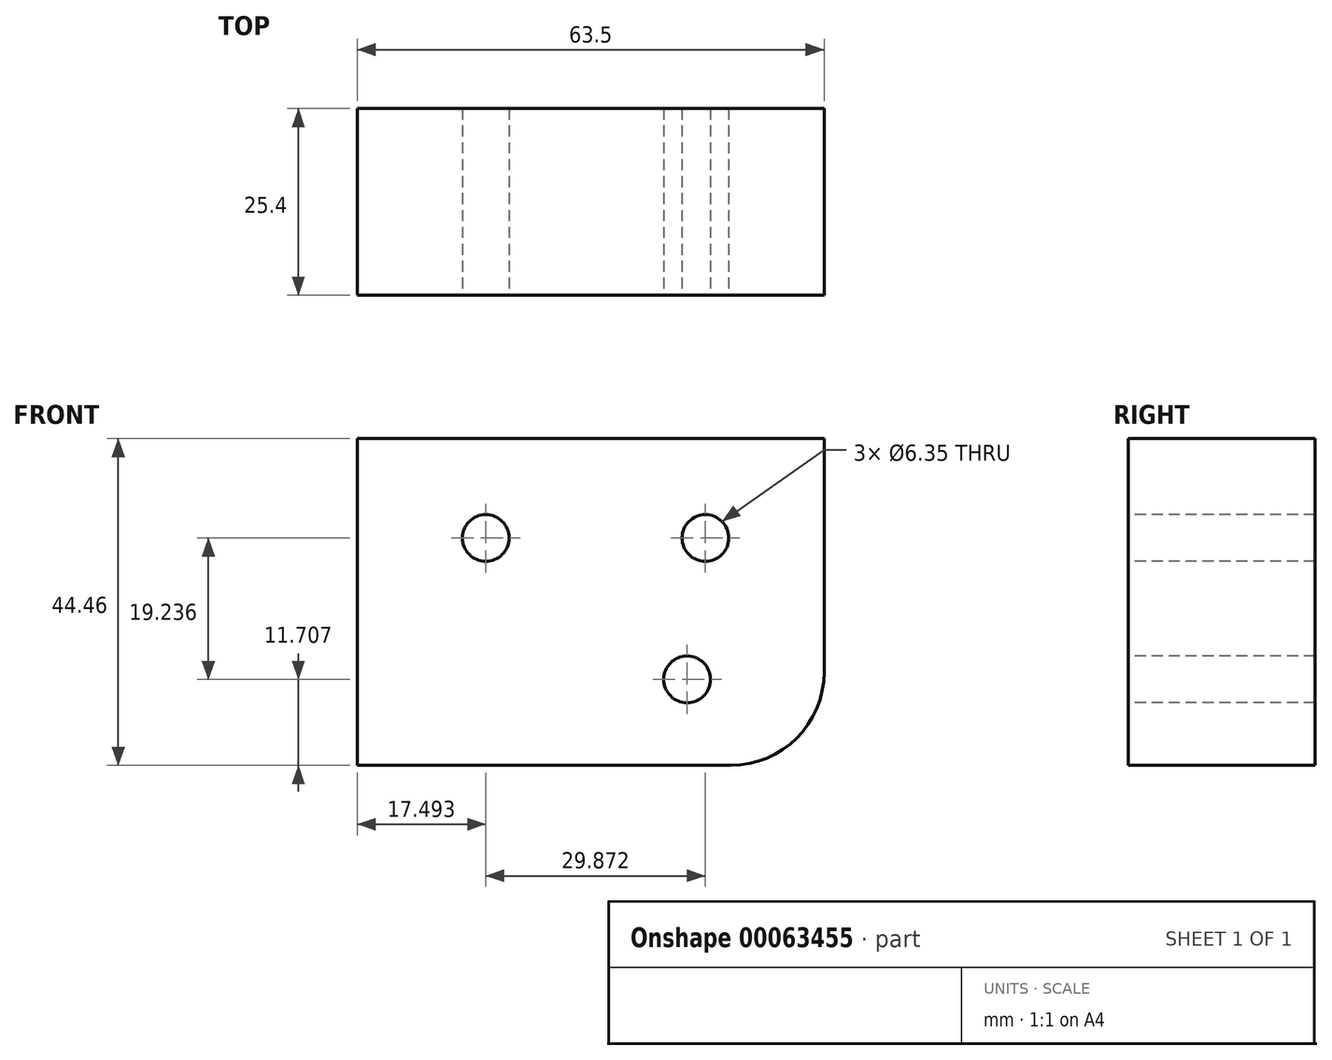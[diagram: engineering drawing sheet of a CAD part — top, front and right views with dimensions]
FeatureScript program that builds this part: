
annotation { "Feature Type Name" : "Feature", "Feature Type Description" : "" }
export const myFeature = defineFeature(function(context is Context, id is Id, definition is map)
    precondition{}
    {
        {
            var Q0;
            Q0=qCreatedBy(makeId("Front.planeOp"),FACE);
            var sketch = newSketch(context, id + "F0", { "sketchPlane" : qUnion([Q0])});
            skLineSegment(sketch, "E0.rect.bottom", {"start": v(19.05, -22.23) * mm, "end": v(-31.75, -22.23) * mm});
            skLineSegment(sketch, "E0.rect.top", {"start": v(31.75, 22.23) * mm, "end": v(-31.75, 22.22) * mm});
            skLineSegment(sketch, "E0.rect.left", {"start": v(31.75, -9.53) * mm, "end": v(31.75, 22.23) * mm});
            skLineSegment(sketch, "E0.rect.right", {"start": v(-31.75, -22.23) * mm, "end": v(-31.75, 22.22) * mm});
            skPoint(sketch, "E0.rect.middle", {"position": v(0, 0) * mm});
            skPoint(sketch, "E1.visualSharp", {"position": v(31.75, -22.23) * mm});
            skArc(sketch, "E1.filletArc", {"start": v(19.05, -22.23) * mm, "mid": v(28.03, -18.5) * mm, "end": v(31.75, -9.53) * mm});
            skSolve(sketch);
        }
        {
            var Q0;
            Q0 = qSketchRegion(id + "F0", true);
            extrude(context, id + "F1", {"entities" : qUnion([Q0]), "depth" : 25.4 * mm});
        }
        {
            var Q0;
            Q0=makeQuery(id+"F1.opExtrude","CAP_FACE",FACE,{"disambiguationData":[OSD([sQuery(id+"F0.wireOp",EDGE,"E0.rect.bottom"),sQuery(id+"F0.wireOp",EDGE,"E0.rect.top"),sQuery(id+"F0.wireOp",EDGE,"E0.rect.left"),sQuery(id+"F0.wireOp",EDGE,"E0.rect.right"),sQuery(id+"F0.wireOp",EDGE,"E1.filletArc")])],"isStart":false});
            var sketch = newSketch(context, id + "F2", { "sketchPlane" : qUnion([Q0])});
            skPoint(sketch, "E2", {"position": v(-14.26, 8.71) * mm});
            skPoint(sketch, "E3", {"position": v(15.61, 8.71) * mm});
            skPoint(sketch, "E4", {"position": v(13.13, -10.52) * mm});
            skSolve(sketch);
        }
        {
            var Q0;
            Q0=sQuery(id+"F2.wireOp",VERTEX,"E2");
            var Q1;
            Q1=sQuery(id+"F2.wireOp",VERTEX,"E3");
            var Q2;
            Q2=sQuery(id+"F2.wireOp",VERTEX,"E4");
            var Q3;
            Q3=makeQuery(id+"F1.opExtrude","SWEPT_BODY",BODY,{"disambiguationData":[OSD([sQuery(id+"F0.wireOp",EDGE,"E0.rect.bottom"),sQuery(id+"F0.wireOp",EDGE,"E0.rect.top"),sQuery(id+"F0.wireOp",EDGE,"E0.rect.left"),sQuery(id+"F0.wireOp",EDGE,"E0.rect.right"),sQuery(id+"F0.wireOp",EDGE,"E1.filletArc")])]});
            hole(context, id + "F3", {"style" : HoleStyle.SIMPLE, "holeDiameter" : 6.35 * mm, "endStyle" : HoleEndStyle.THROUGH, "locations" : qUnion([Q0, Q1, Q2]), "scope" : qUnion([Q3])});
        }
    });
